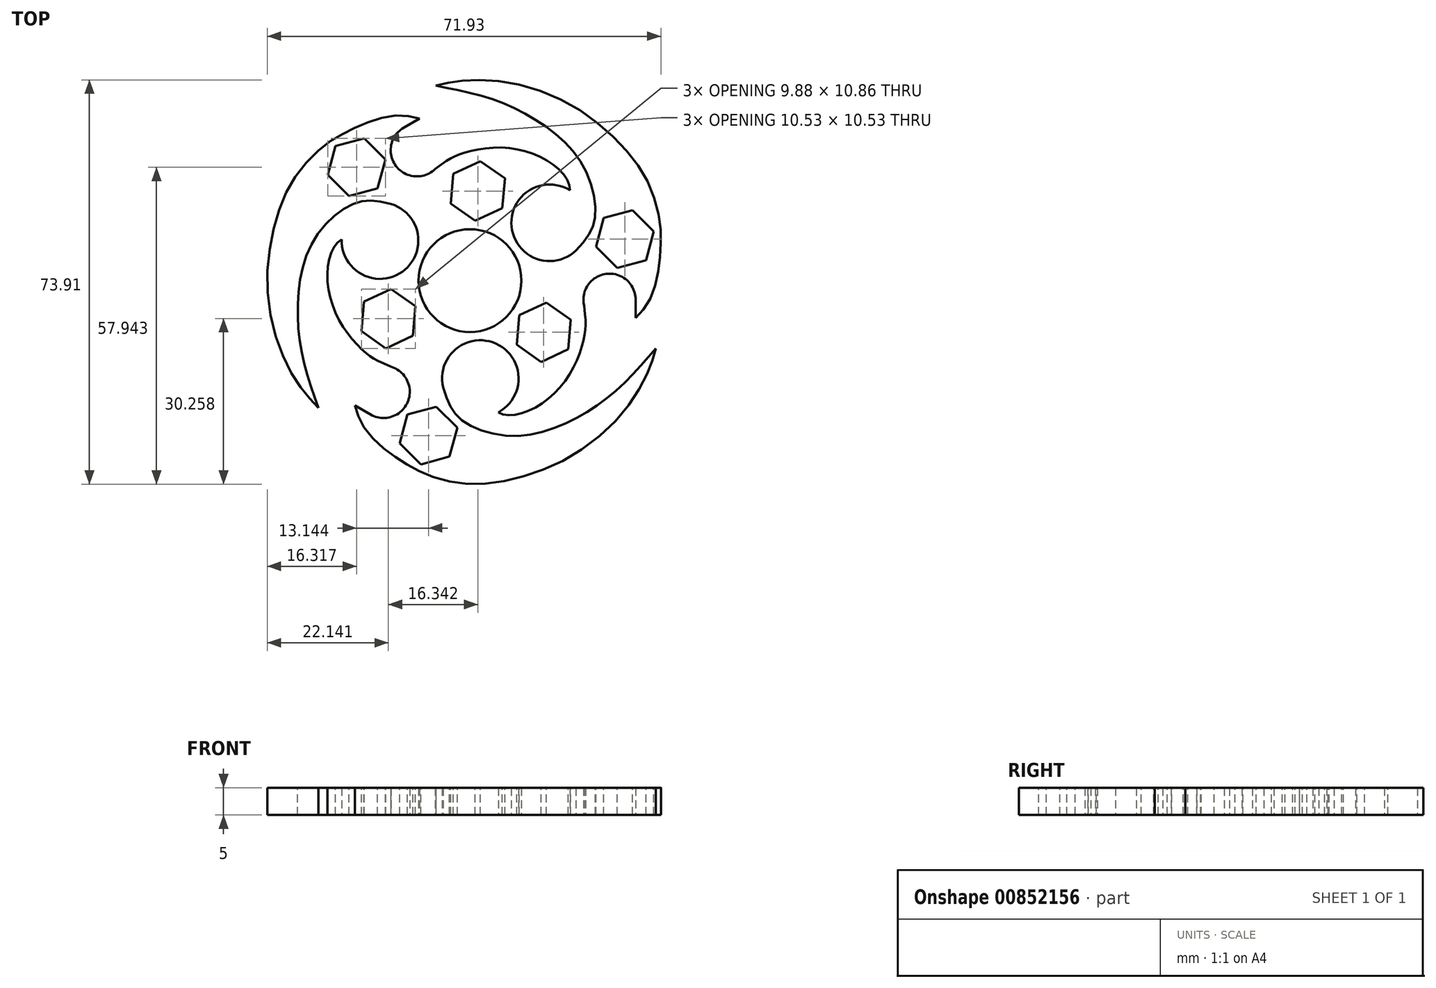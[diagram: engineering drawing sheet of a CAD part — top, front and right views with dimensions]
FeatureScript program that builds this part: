
annotation { "Feature Type Name" : "Feature", "Feature Type Description" : "" }
export const myFeature = defineFeature(function(context is Context, id is Id, definition is map)
    precondition{}
    {
        {
            var Q0;
            Q0=qCreatedBy(makeId("Top.planeOp"),FACE);
            var sketch = newSketch(context, id + "F0", { "sketchPlane" : qUnion([Q0])});
            skCircle(sketch, "E0", {"center": v(0, 0) * mm, "radius": 9.4 * mm, "construction": true});
            skCircle(sketch, "E1", {"center": v(0, 0) * mm, "radius": 11 * mm, "construction": true});
            skPoint(sketch, "E2.orphan", {"position": v(-0.16, 0.1) * mm});
            skLineSegment(sketch, "E3", {"start": v(0, 0) * mm, "end": v(54.2, 0) * mm, "construction": true});
            skLineSegment(sketch, "E4", {"start": v(0, 0) * mm, "end": v(46.96, 34.12) * mm, "construction": true});
            skPoint(sketch, "E5", {"position": v(18.27, 16.52) * mm});
            skPoint(sketch, "E6", {"position": v(19.37, 5.5) * mm});
            skFitSpline(sketch, "E7", {"points": [v(18.27, 16.52) * mm, v(14.9, 21.44) * mm, v(5.63, 24.33) * mm, v(-2.05, 23.03) * mm, v(-6.38, 20.42) * mm], "startDerivative": vector(1.06, 21.36) * mm, "endDerivative": vector(-29.74, -21.68) * mm});
            skPoint(sketch, "E8", {"position": v(-12.46, 27.57) * mm});
            skLineSegment(sketch, "E9", {"start": v(-12.46, 27.57) * mm, "end": v(-9.25, 29.62) * mm});
            skArc(sketch, "E10", {"start": v(-12.46, 27.57) * mm, "mid": v(-13.51, 20.5) * mm, "end": v(-6.38, 20.42) * mm, "construction": true});
            skLineSegment(sketch, "E11", {"start": v(-9.25, 29.62) * mm, "end": v(0, 0) * mm, "construction": true});
            skLineSegment(sketch, "E12", {"start": v(0, 0) * mm, "end": v(20.87, -4.69) * mm, "construction": true});
            skFitSpline(sketch, "E13", {"points": [v(19.37, 5.5) * mm, v(22.8, 11.23) * mm, v(20.76, 20.87) * mm, v(13.06, 28.72) * mm, v(3.47, 33.38) * mm, v(-6.26, 35.63) * mm], "startDerivative": vector(34.03, 36.44) * mm, "endDerivative": vector(-46.4, 9.15) * mm});
            skArc(sketch, "E14", {"start": v(18.27, 16.52) * mm, "mid": v(7.6, 9.88) * mm, "end": v(19.37, 5.5) * mm});
            skFitSpline(sketch, "E15", {"points": [v(-6.26, 35.63) * mm, v(-1.76, 36.51) * mm, v(6.78, 36.27) * mm, v(18.35, 32.18) * mm, v(27.26, 25.2) * mm, v(32.47, 18.1) * mm, v(34.65, 10.9) * mm, v(34.83, 5.8) * mm, v(34.23, 0.68) * mm, v(32.5, -4.12) * mm, v(30.28, -6.8) * mm], "startDerivative": vector(50.97, 12.47) * mm, "endDerivative": vector(-33.27, -33.38) * mm});
            skPoint(sketch, "E16", {"position": v(-5.18, 7.84) * mm});
            skPoint(sketch, "E17", {"position": v(9.17, -2.06) * mm});
            skArc(sketch, "E18", {"start": v(-5.18, 7.84) * mm, "mid": v(5.34, 7.74) * mm, "end": v(9.17, -2.06) * mm});
            skLineSegment(sketch, "E19", {"start": v(9.17, -2.06) * mm, "end": v(20.87, -4.69) * mm});
            skPoint(sketch, "E20", {"position": v(20.87, -4.69) * mm});
            skLineSegment(sketch, "E21", {"start": v(30.28, -6.8) * mm, "end": v(30.28, -3.5) * mm});
            skArc(sketch, "E22", {"start": v(30.28, -3.5) * mm, "mid": v(24.9, 1.24) * mm, "end": v(20.87, -4.69) * mm});
            skLineSegment(sketch, "E23", {"start": v(-6.38, 20.42) * mm, "end": v(0, 0) * mm});
            skSolve(sketch);
        }
        {
            var Q0;
            {var subQ1=sQuery(id+"F0.wireOp",EDGE,"E7");Q0=makeQuery(id+"F0.imprint","IMPRINT",FACE,{"disambiguationData":[TD([[makeQuery(id+"F0.imprint","IMPRINT",EDGE,{"derivedFrom":subQ1}),1.0]])]});}
            var Q1;
            {var subQ3=sQuery(id+"F0.wireOp",EDGE,"vHKPbalO-4eth-BBEX-WpL6-SEu3oY2ButND");Q1=makeQuery(id+"F0.imprint","IMPRINT",FACE,{"disambiguationData":[TD([[makeQuery(id+"F0.imprint","IMPRINT",EDGE,{"derivedFrom":subQ3}),-1.0]])]});}
            extrude(context, id + "F1", {"entities" : qUnion([Q0, Q1]), "depth" : 5 * mm, "offsetDistance" : 25 * mm});
        }
        {
            var Q0;
            Q0=qCreatedBy(makeId("Front.planeOp"),FACE);
            var sketch = newSketch(context, id + "F2", { "sketchPlane" : qUnion([Q0])});
            skLineSegment(sketch, "E24", {"start": v(0, 0) * mm, "end": v(0, 55.86) * mm, "construction": true});
            skSolve(sketch);
        }
        {
            var Q0;
            Q0=makeQuery(id+"F1.opExtrude","SWEPT_BODY",BODY,{"disambiguationData":[OSD([sQuery(id+"F0.wireOp",EDGE,"E10"),sQuery(id+"F0.wireOp",EDGE,"zojvIL6C-BE0k-co1T-s1hC-A86PAPgQTmRn"),sQuery(id+"F0.wireOp",EDGE,"vHKPbalO-4eth-BBEX-WpL6-SEu3oY2ButND")])]});
            var Q1;
            Q1=makeQuery(id+"F1.opExtrude","SWEPT_BODY",BODY,{"disambiguationData":[OSD([sQuery(id+"F0.wireOp",EDGE,"E7"),sQuery(id+"F0.wireOp",EDGE,"E10"),sQuery(id+"F0.wireOp",EDGE,"E13"),sQuery(id+"F0.wireOp",EDGE,"E14"),sQuery(id+"F0.wireOp",EDGE,"E15"),sQuery(id+"F0.wireOp",EDGE,"E18"),sQuery(id+"F0.wireOp",EDGE,"7hLGK6TZ-VlNH-Qm4p-4Afw-j84KGP8fiYRH"),sQuery(id+"F0.wireOp",EDGE,"E19")])]});
            var Q2;
            Q2=sQuery(id+"F2.wireOp",EDGE,"E24");
            circularPattern(context, id + "F3", {"operationType" : NewBodyOperationType.ADD, "entities" : qUnion([Q0, Q1]), "axis" : qUnion([Q2]), "angle" : 360 * degree, "instanceCount" : 3, "equalSpace" : true});
        }
        {
            var Q0;
            {var subQ0=makeQuery(id+"F1.opExtrude","CAP_FACE",FACE,{"disambiguationData":[OSD([sQuery(id+"F0.wireOp",EDGE,"E7"),sQuery(id+"F0.wireOp",EDGE,"E13"),sQuery(id+"F0.wireOp",EDGE,"E14"),sQuery(id+"F0.wireOp",EDGE,"E15"),sQuery(id+"F0.wireOp",EDGE,"E18"),sQuery(id+"F0.wireOp",EDGE,"E19"),sQuery(id+"F0.wireOp",EDGE,"E21"),sQuery(id+"F0.wireOp",EDGE,"E22"),sQuery(id+"F0.wireOp",EDGE,"E23")])],"isStart":false});Q0=makeQuery(id+"F3.boolean.opBoolean","MERGE",FACE,{"derivedFrom":[subQ0,makeQuery(id+"F3.opPattern","COPY",FACE,{"derivedFrom":subQ0,"instanceName":"1"}),makeQuery(id+"F3.opPattern","COPY",FACE,{"derivedFrom":subQ0,"instanceName":"2"})]});}
            var sketch = newSketch(context, id + "F4", { "sketchPlane" : qUnion([Q0])});
            skLineSegment(sketch, "E25", {"start": v(0, 0) * mm, "end": v(5, 57.07) * mm, "construction": true});
            skLineSegment(sketch, "E26", {"start": v(0, 0) * mm, "end": v(72.72, -50.92) * mm, "construction": true});
            skCircle(sketch, "E27.cCircle", {"center": v(1.43, 16.39) * mm, "radius": 5.45 * mm, "construction": true});
            skLineSegment(sketch, "E27.0", {"start": v(0.96, 10.96) * mm, "end": v(-3.5, 14.08) * mm});
            skLineSegment(sketch, "E27.1", {"start": v(-3.5, 14.08) * mm, "end": v(-3.03, 19.51) * mm});
            skLineSegment(sketch, "E27.2", {"start": v(-3.03, 19.51) * mm, "end": v(1.9, 21.82) * mm});
            skLineSegment(sketch, "E27.3", {"start": v(1.9, 21.82) * mm, "end": v(6.37, 18.7) * mm});
            skLineSegment(sketch, "E27.4", {"start": v(6.37, 18.7) * mm, "end": v(5.9, 13.26) * mm});
            skLineSegment(sketch, "E27.5", {"start": v(5.9, 13.26) * mm, "end": v(0.96, 10.96) * mm});
            skLineSegment(sketch, "E28.1.0", {"start": v(-19.85, -9.26) * mm, "end": v(-19.37, -3.83) * mm});
            skLineSegment(sketch, "E28.1.1", {"start": v(-19.37, -3.83) * mm, "end": v(-14.43, -1.52) * mm});
            skLineSegment(sketch, "E28.1.2", {"start": v(-14.43, -1.52) * mm, "end": v(-9.97, -4.65) * mm});
            skLineSegment(sketch, "E28.1.3", {"start": v(-9.97, -4.65) * mm, "end": v(-10.44, -10.08) * mm});
            skLineSegment(sketch, "E28.1.4", {"start": v(-10.44, -10.08) * mm, "end": v(-15.38, -12.38) * mm});
            skLineSegment(sketch, "E28.1.5", {"start": v(-15.38, -12.38) * mm, "end": v(-19.85, -9.26) * mm});
            skLineSegment(sketch, "E28.2.0", {"start": v(17.94, -12.56) * mm, "end": v(13, -14.86) * mm});
            skLineSegment(sketch, "E28.2.1", {"start": v(13, -14.86) * mm, "end": v(8.54, -11.74) * mm});
            skLineSegment(sketch, "E28.2.2", {"start": v(8.54, -11.74) * mm, "end": v(9.01, -6.3) * mm});
            skLineSegment(sketch, "E28.2.3", {"start": v(9.01, -6.3) * mm, "end": v(13.95, -4) * mm});
            skLineSegment(sketch, "E28.2.4", {"start": v(13.95, -4) * mm, "end": v(18.41, -7.13) * mm});
            skLineSegment(sketch, "E28.2.5", {"start": v(18.41, -7.13) * mm, "end": v(17.94, -12.56) * mm});
            skPoint(sketch, "E28.center", {"position": v(0, 0) * mm});
            skLineSegment(sketch, "E29", {"start": v(0, 0) * mm, "end": v(42.82, 11.47) * mm, "construction": true});
            skCircle(sketch, "E30.cCircle", {"center": v(28.32, 7.59) * mm, "radius": 5.45 * mm, "construction": true});
            skLineSegment(sketch, "E30.0", {"start": v(33.59, 9) * mm, "end": v(32.18, 3.73) * mm});
            skLineSegment(sketch, "E30.1", {"start": v(32.18, 3.73) * mm, "end": v(26.91, 2.32) * mm});
            skLineSegment(sketch, "E30.2", {"start": v(26.91, 2.32) * mm, "end": v(23.06, 6.18) * mm});
            skLineSegment(sketch, "E30.3", {"start": v(23.06, 6.18) * mm, "end": v(24.47, 11.44) * mm});
            skLineSegment(sketch, "E30.4", {"start": v(24.47, 11.44) * mm, "end": v(29.73, 12.85) * mm});
            skLineSegment(sketch, "E30.5", {"start": v(29.73, 12.85) * mm, "end": v(33.59, 9) * mm});
            skLineSegment(sketch, "E31.1.0", {"start": v(-24.59, 24.59) * mm, "end": v(-19.32, 26) * mm});
            skLineSegment(sketch, "E31.1.1", {"start": v(-26, 19.32) * mm, "end": v(-24.59, 24.59) * mm});
            skLineSegment(sketch, "E31.1.2", {"start": v(-22.14, 15.47) * mm, "end": v(-26, 19.32) * mm});
            skLineSegment(sketch, "E31.1.3", {"start": v(-16.88, 16.88) * mm, "end": v(-22.14, 15.47) * mm});
            skLineSegment(sketch, "E31.1.4", {"start": v(-15.47, 22.14) * mm, "end": v(-16.88, 16.88) * mm});
            skLineSegment(sketch, "E31.1.5", {"start": v(-19.32, 26) * mm, "end": v(-15.47, 22.14) * mm});
            skLineSegment(sketch, "E31.2.0", {"start": v(-9, -33.59) * mm, "end": v(-12.85, -29.73) * mm});
            skLineSegment(sketch, "E31.2.1", {"start": v(-3.73, -32.18) * mm, "end": v(-9, -33.59) * mm});
            skLineSegment(sketch, "E31.2.2", {"start": v(-2.32, -26.91) * mm, "end": v(-3.73, -32.18) * mm});
            skLineSegment(sketch, "E31.2.3", {"start": v(-6.18, -23.06) * mm, "end": v(-2.32, -26.91) * mm});
            skLineSegment(sketch, "E31.2.4", {"start": v(-11.44, -24.47) * mm, "end": v(-6.18, -23.06) * mm});
            skLineSegment(sketch, "E31.2.5", {"start": v(-12.85, -29.73) * mm, "end": v(-11.44, -24.47) * mm});
            skSolve(sketch);
        }
        {
            var Q0;
            Q0=makeQuery(id+"F4.imprint","IMPRINT",FACE,{"disambiguationData":[TD([[makeQuery(id+"F4.imprint","IMPRINT",EDGE,{"derivedFrom":sQuery(id+"F4.wireOp",EDGE,"E27.0")}),-1.0]])]});
            var Q1;
            Q1=makeQuery(id+"F4.imprint","IMPRINT",FACE,{"disambiguationData":[TD([[makeQuery(id+"F4.imprint","IMPRINT",EDGE,{"derivedFrom":sQuery(id+"F4.wireOp",EDGE,"E28.2.0")}),-1.0]])]});
            var Q2;
            Q2=makeQuery(id+"F4.imprint","IMPRINT",FACE,{"disambiguationData":[TD([[makeQuery(id+"F4.imprint","IMPRINT",EDGE,{"derivedFrom":sQuery(id+"F4.wireOp",EDGE,"E28.1.0")}),-1.0]])]});
            extrude(context, id + "F5", {"entities" : qUnion([Q0, Q1, Q2]), "operationType" : NewBodyOperationType.REMOVE, "oppositeDirection" : true, "depth" : 25 * mm, "offsetDistance" : 25 * mm});
        }
        {
            var Q0;
            Q0=makeQuery(id+"F4.imprint","IMPRINT",FACE,{"disambiguationData":[TD([[makeQuery(id+"F4.imprint","IMPRINT",EDGE,{"derivedFrom":sQuery(id+"F4.wireOp",EDGE,"E31.1.0")}),-1.0]])]});
            var Q1;
            Q1=makeQuery(id+"F4.imprint","IMPRINT",FACE,{"disambiguationData":[TD([[makeQuery(id+"F4.imprint","IMPRINT",EDGE,{"derivedFrom":sQuery(id+"F4.wireOp",EDGE,"E30.0")}),-1.0]])]});
            var Q2;
            Q2=makeQuery(id+"F4.imprint","IMPRINT",FACE,{"disambiguationData":[TD([[makeQuery(id+"F4.imprint","IMPRINT",EDGE,{"derivedFrom":sQuery(id+"F4.wireOp",EDGE,"E31.2.0")}),-1.0]])]});
            extrude(context, id + "F6", {"entities" : qUnion([Q0, Q1, Q2]), "operationType" : NewBodyOperationType.REMOVE, "oppositeDirection" : true, "depth" : 25 * mm, "offsetDistance" : 25 * mm});
        }
    });
